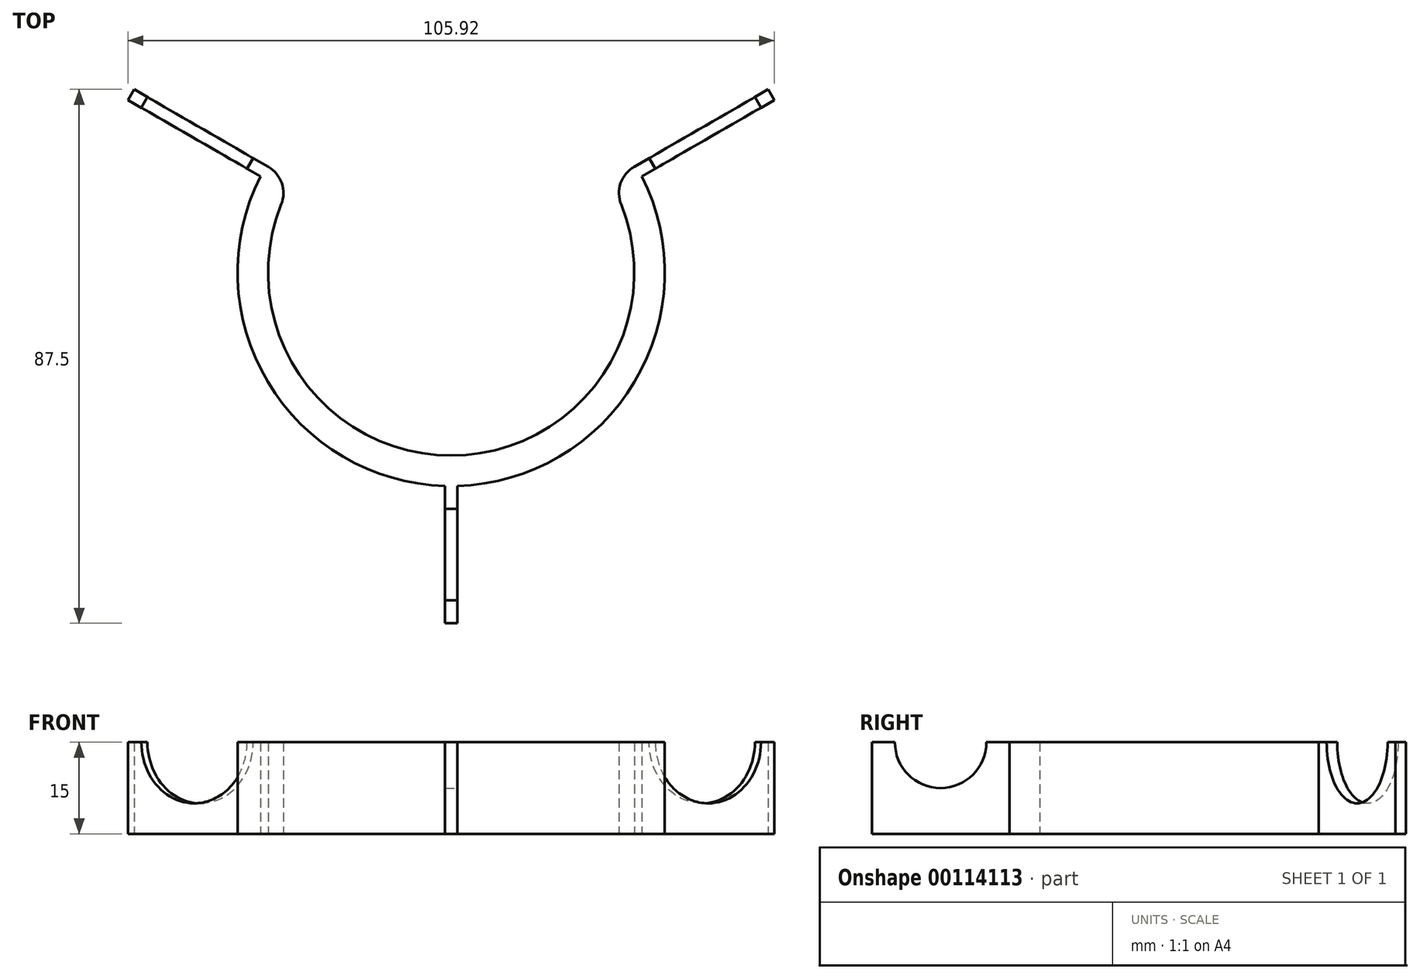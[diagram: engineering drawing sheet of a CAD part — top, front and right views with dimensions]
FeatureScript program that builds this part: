
annotation { "Feature Type Name" : "Feature", "Feature Type Description" : "" }
export const myFeature = defineFeature(function(context is Context, id is Id, definition is map)
    precondition{}
    {
        {
            var Q0;
            Q0=qCreatedBy(makeId("Top.planeOp"),FACE);
            var sketch = newSketch(context, id + "F0", { "sketchPlane" : qUnion([Q0])});
            skLineSegment(sketch, "E0", {"start": v(0, 0) * mm, "end": v(-30.31, 17.5) * mm, "construction": true});
            skLineSegment(sketch, "E1", {"start": v(0, 0) * mm, "end": v(0, 71.1) * mm, "construction": true});
            skLineSegment(sketch, "E2", {"start": v(-30.31, 17.5) * mm, "end": v(-25.98, 15) * mm});
            skArc(sketch, "E3", {"start": v(-25.98, 15) * mm, "mid": v(0, -30) * mm, "end": v(25.98, 15) * mm});
            skArc(sketch, "E4", {"start": v(-30.31, 17.5) * mm, "mid": v(0, -35) * mm, "end": v(30.31, 17.5) * mm});
            skLineSegment(sketch, "E5", {"start": v(-30.31, 17.5) * mm, "end": v(-51.96, 30) * mm});
            skLineSegment(sketch, "E6", {"start": v(-51.96, 30) * mm, "end": v(-52.96, 28.27) * mm});
            skLineSegment(sketch, "E7", {"start": v(-52.96, 28.27) * mm, "end": v(-31.26, 15.74) * mm});
            skPoint(sketch, "E8", {"position": v(0, -32.5) * mm});
            skLineSegment(sketch, "E9.bottom", {"start": v(-1, -32.5) * mm, "end": v(1, -32.5) * mm});
            skLineSegment(sketch, "E9.top", {"start": v(-1, -57.5) * mm, "end": v(1, -57.5) * mm});
            skLineSegment(sketch, "E9.left", {"start": v(-1, -32.5) * mm, "end": v(-1, -57.5) * mm});
            skLineSegment(sketch, "E9.right", {"start": v(1, -32.5) * mm, "end": v(1, -57.5) * mm});
            skLineSegment(sketch, "E10.MirrorCS", {"start": v(30.31, 17.5) * mm, "end": v(51.96, 30) * mm});
            skLineSegment(sketch, "E11.MirrorCS", {"start": v(52.96, 28.27) * mm, "end": v(31.26, 15.74) * mm});
            skLineSegment(sketch, "E12.MirrorCS", {"start": v(51.96, 30) * mm, "end": v(52.96, 28.27) * mm});
            skLineSegment(sketch, "E13.MirrorCS", {"start": v(0, 0) * mm, "end": v(30.31, 17.5) * mm, "construction": true});
            skLineSegment(sketch, "E14", {"start": v(30.31, 17.5) * mm, "end": v(25.98, 15) * mm});
            skLineSegment(sketch, "E15", {"start": v(0, -30) * mm, "end": v(0, -35) * mm, "construction": true});
            skSolve(sketch);
        }
        {
            var Q0;
            Q0 = qSketchRegion(id + "F0", true);
            extrude(context, id + "F1", {"entities" : qUnion([Q0]), "depth" : 15 * mm});
        }
        {
            var Q0;
            Q0=makeQuery(id+"F1.opExtrude","SWEPT_FACE",FACE,{"disambiguationData":[OSD([sQuery(id+"F0.wireOp",EDGE,"E7")])]});
            var sketch = newSketch(context, id + "F2", { "sketchPlane" : qUnion([Q0])});
            skArc(sketch, "E16", {"start": v(-57.47, 15) * mm, "mid": v(-47.47, 5) * mm, "end": v(-37.47, 15) * mm});
            skLineSegment(sketch, "E17", {"start": v(-57.47, 15) * mm, "end": v(-37.47, 15) * mm});
            skSolve(sketch);
        }
        {
            var Q0;
            Q0=makeQuery(id+"F2.imprint","IMPRINT",FACE,{"disambiguationData":[TD([[makeQuery(id+"F2.imprint","IMPRINT",EDGE,{"derivedFrom":sQuery(id+"F2.wireOp",EDGE,"E16")}),1.0]])]});
            extrude(context, id + "F3", {"entities" : qUnion([Q0]), "operationType" : NewBodyOperationType.REMOVE, "endBound" : BoundingType.THROUGH_ALL, "oppositeDirection" : true, "depth" : 25 * mm});
        }
        {
            var Q0;
            Q0=makeQuery(id+"F1.opExtrude","SWEPT_FACE",FACE,{"disambiguationData":[OSD([sQuery(id+"F0.wireOp",EDGE,"E11.MirrorCS")])]});
            var sketch = newSketch(context, id + "F4", { "sketchPlane" : qUnion([Q0])});
            skArc(sketch, "E18", {"start": v(37.47, 15) * mm, "mid": v(47.47, 5) * mm, "end": v(57.47, 15) * mm});
            skLineSegment(sketch, "E19", {"start": v(37.47, 15) * mm, "end": v(57.47, 15) * mm});
            skSolve(sketch);
        }
        {
            var Q0;
            Q0 = qSketchRegion(id + "F4", true);
            extrude(context, id + "F5", {"entities" : qUnion([Q0]), "operationType" : NewBodyOperationType.REMOVE, "endBound" : BoundingType.THROUGH_ALL, "oppositeDirection" : true, "depth" : 25 * mm});
        }
        {
            var Q0;
            Q0=makeQuery(id+"F1.opExtrude","SWEPT_FACE",FACE,{"disambiguationData":[OSD([sQuery(id+"F0.wireOp",EDGE,"E9.right")])]});
            var sketch = newSketch(context, id + "F6", { "sketchPlane" : qUnion([Q0])});
            skArc(sketch, "E20", {"start": v(-53.74, 15) * mm, "mid": v(-46.24, 7.5) * mm, "end": v(-38.74, 15) * mm});
            skLineSegment(sketch, "E21", {"start": v(-53.74, 15) * mm, "end": v(-38.74, 15) * mm});
            skSolve(sketch);
        }
        {
            var Q0;
            Q0 = qSketchRegion(id + "F6", true);
            extrude(context, id + "F7", {"entities" : qUnion([Q0]), "operationType" : NewBodyOperationType.REMOVE, "endBound" : BoundingType.THROUGH_ALL, "oppositeDirection" : true, "depth" : 25 * mm});
        }
        {
            var Q0;
            Q0=makeQuery(id+"F1.opExtrude","SWEPT_EDGE",EDGE,{"disambiguationData":[OSD([sQuery(id+"F0.wireOp",EDGE,"E2"),sQuery(id+"F0.wireOp",EDGE,"E3")])]});
            var Q1;
            Q1=makeQuery(id+"F1.opExtrude","SWEPT_EDGE",EDGE,{"disambiguationData":[OSD([sQuery(id+"F0.wireOp",EDGE,"E3"),sQuery(id+"F0.wireOp",EDGE,"E14")])]});
            fillet(context, id + "F8", {"entities" : qUnion([Q0, Q1]), "radius" : 5 * mm, "tangentPropagation" : true, "allowEdgeOverflow" : false});
        }
    });
